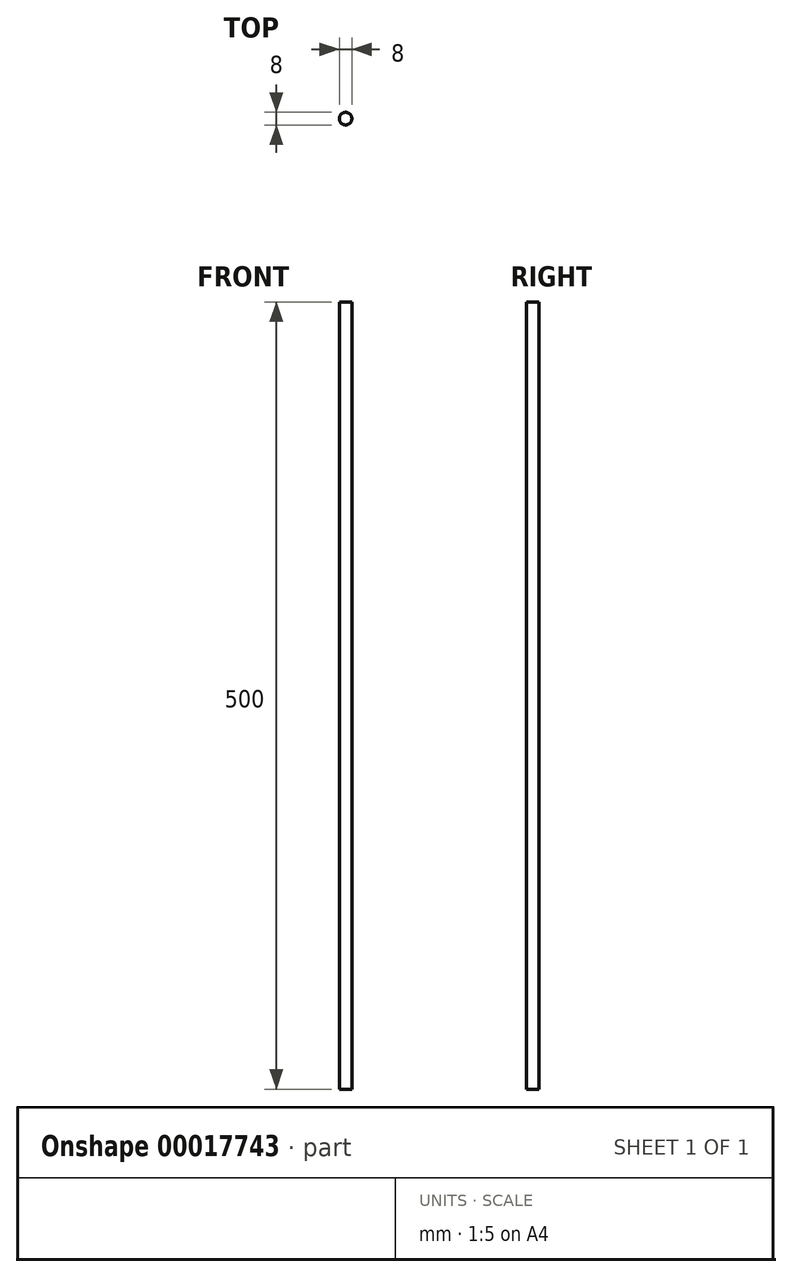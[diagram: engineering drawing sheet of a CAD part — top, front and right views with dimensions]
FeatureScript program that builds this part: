
annotation { "Feature Type Name" : "Feature", "Feature Type Description" : "" }
export const myFeature = defineFeature(function(context is Context, id is Id, definition is map)
    precondition{}
    {
        {
            var Q0;
            Q0=qCreatedBy(makeId("Top.planeOp"),FACE);
            var sketch = newSketch(context, id + "F0", { "sketchPlane" : qUnion([Q0])});
            skCircle(sketch, "E0", {"center": v(0, 0) * mm, "radius": 4 * mm});
            skSolve(sketch);
        }
        {
            var Q0;
            Q0=qSketchRegion(id+"F0",true);
            extrude(context, id + "F1", {"entities" : qUnion([Q0]), "depth" : 500 * mm});
        }
    });
